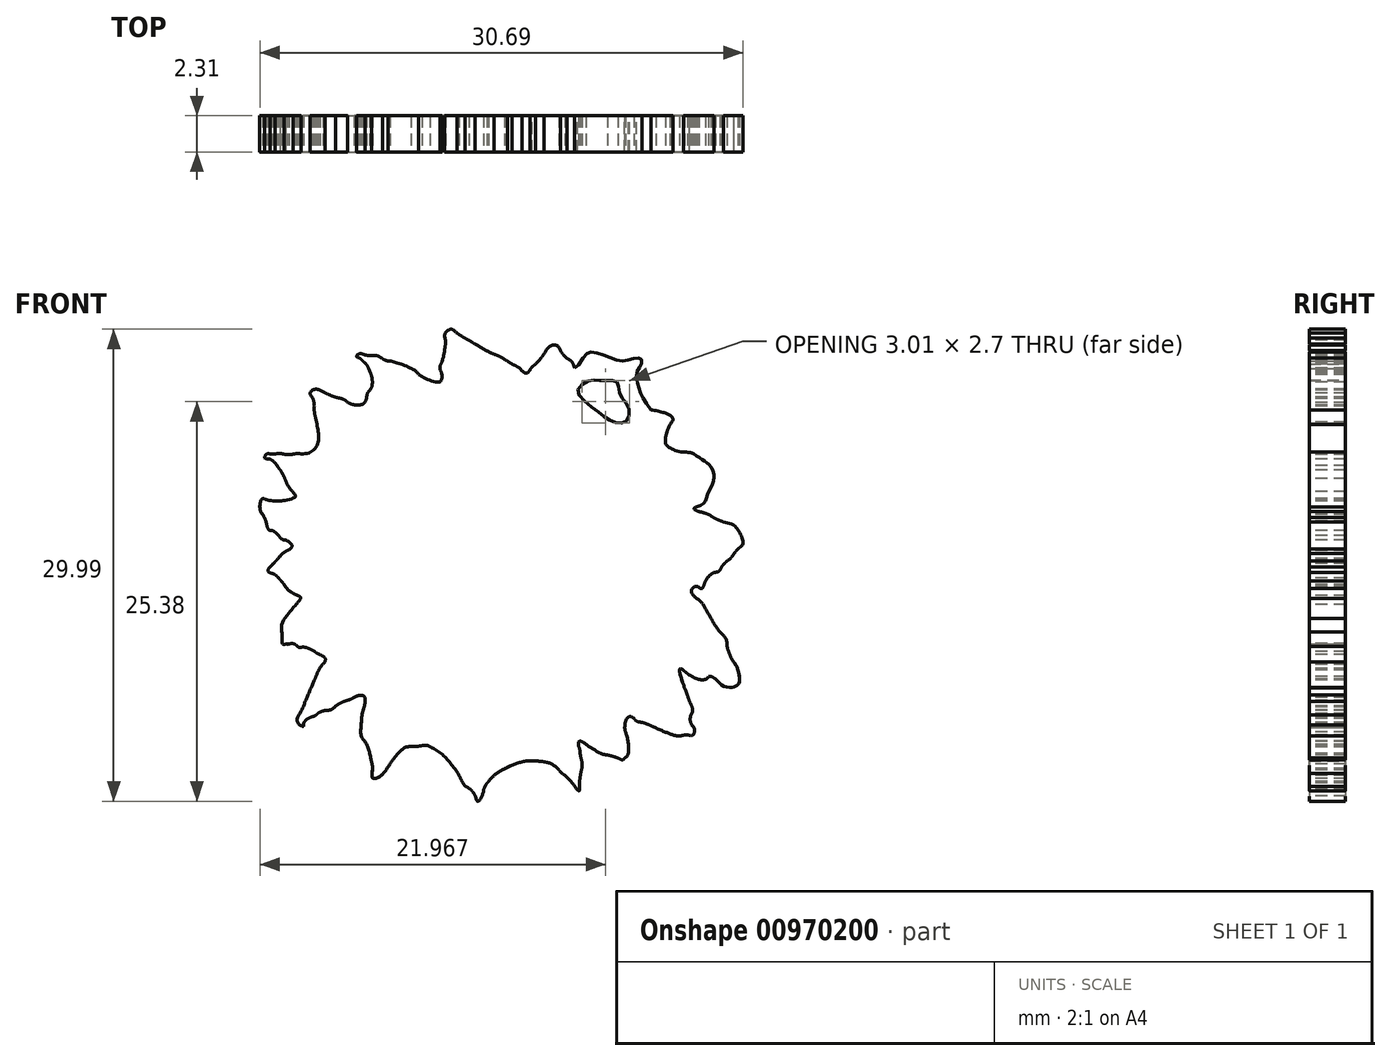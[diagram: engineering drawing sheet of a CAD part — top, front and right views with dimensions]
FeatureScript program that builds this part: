
annotation { "Feature Type Name" : "Feature", "Feature Type Description" : "" }
export const myFeature = defineFeature(function(context is Context, id is Id, definition is map)
    precondition{}
    {
        {
            var Q0;
            Q0=qCreatedBy(makeId("Front.planeOp"),FACE);
            var sketch = newSketch(context, id + "F0", { "sketchPlane" : qUnion([Q0])});
            skFitSpline(sketch, "E0", {"points": [v(2.12, 9.55) * mm, v(2.44, 9.4) * mm, v(2.83, 9.1) * mm, v(3.27, 8.7) * mm, v(3.44, 8.3) * mm, v(3.76, 7.75) * mm, v(3.76, 7.23) * mm, v(3.37, 6.8) * mm, v(2.85, 6.34) * mm, v(2.33, 5.86) * mm, v(1.64, 5.47) * mm, v(1.23, 5.23) * mm, v(0.6, 5.34) * mm, v(0.01, 5.58) * mm, v(-0.53, 5.65) * mm, v(-1, 5.84) * mm, v(-1.7, 6.08) * mm, v(-2.35, 6.32) * mm, v(-2.79, 6.5) * mm, v(-2.7, 6.82) * mm, v(-2.27, 7.1) * mm, v(-1.72, 7.4) * mm, v(-1.1, 7.27) * mm, v(-0.1, 7) * mm, v(0.92, 6.45) * mm, v(1.55, 6.32) * mm, v(2.16, 6.51) * mm, v(2.29, 6.88) * mm, v(1.9, 7.36) * mm, v(1.55, 7.66) * mm, v(1.25, 8.23) * mm, v(1.03, 8.62) * mm, v(1.03, 8.99) * mm, v(1.33, 9.18) * mm, v(1.86, 9.36) * mm, v(2.12, 9.55) * mm]});
            skFitSpline(sketch, "E1", {"points": [v(5.07, 10.48) * mm, v(5.98, 10.53) * mm, v(6.8, 10.57) * mm, v(7.37, 10.6) * mm, v(7.86, 10.57) * mm, v(8.45, 10.53) * mm, v(9.01, 10.61) * mm, v(9.66, 10.48) * mm, v(10.1, 10.33) * mm, v(10.1, 9.8) * mm, v(10.06, 9.07) * mm, v(9.86, 8.64) * mm, v(9.45, 8.62) * mm, v(8.69, 8.84) * mm, v(8.12, 8.88) * mm, v(7.3, 8.88) * mm, v(6.45, 8.73) * mm, v(5.76, 8.58) * mm, v(5.33, 8.36) * mm, v(4.76, 8.1) * mm, v(4.63, 8.53) * mm, v(4.35, 8.9) * mm, v(4.02, 9.31) * mm, v(3.76, 9.7) * mm, v(3.72, 10.07) * mm, v(4, 10.27) * mm, v(4.55, 10.38) * mm, v(5.07, 10.48) * mm]});
            skFitSpline(sketch, "E2", {"points": [v(3.8, 5.84) * mm, v(3.42, 5.5) * mm, v(3.11, 5.02) * mm, v(2.74, 4.7) * mm, v(2.81, 4.35) * mm, v(3.29, 4.04) * mm, v(3.85, 3.8) * mm, v(4.5, 3.48) * mm, v(5.17, 3.28) * mm, v(5.63, 3.15) * mm, v(5.98, 3.46) * mm, v(6.28, 3.59) * mm, v(6.41, 3.76) * mm, v(6.22, 4.28) * mm, v(5.67, 4.8) * mm, v(5.41, 5.32) * mm, v(5.02, 5.84) * mm, v(4.78, 6.15) * mm, v(4.46, 6.28) * mm, v(3.8, 5.84) * mm]});
            skFitSpline(sketch, "E3", {"points": [v(7.84, 7.7) * mm, v(8.28, 7.8) * mm, v(9.08, 7.64) * mm, v(9.64, 7.37) * mm, v(9.73, 6.97) * mm, v(9.58, 6.5) * mm, v(9.45, 5.82) * mm, v(9.32, 5.32) * mm, v(9.25, 4.87) * mm, v(9.23, 4.32) * mm, v(9.08, 3.8) * mm, v(8.88, 3.5) * mm, v(8.4, 3.43) * mm, v(8.02, 3.85) * mm, v(7.5, 4.54) * mm, v(7.08, 5.06) * mm, v(6.56, 5.71) * mm, v(6.26, 6.38) * mm, v(6.04, 6.9) * mm, v(6.28, 7.23) * mm, v(6.54, 7.47) * mm, v(7.15, 7.7) * mm, v(7.84, 7.7) * mm]});
            skFitSpline(sketch, "E4", {"points": [v(12.28, 5.84) * mm, v(13.03, 5.31) * mm, v(13.8, 4.47) * mm, v(14.16, 4.05) * mm, v(13.98, 3.67) * mm, v(13, 3.38) * mm, v(12.17, 2.87) * mm, v(11.6, 2.58) * mm, v(10.93, 2.43) * mm, v(10.57, 2.67) * mm, v(10.35, 2.9) * mm, v(10.31, 3.45) * mm, v(10.28, 4.15) * mm, v(10.57, 4.84) * mm, v(10.72, 5.84) * mm, v(10.86, 6.5) * mm, v(11.04, 7.03) * mm, v(11.28, 6.8) * mm, v(11.85, 6.24) * mm, v(12.28, 5.84) * mm]});
            skFitSpline(sketch, "E5", {"points": [v(14.32, 7.37) * mm, v(14.83, 6.85) * mm, v(15.37, 6.41) * mm, v(15.91, 5.84) * mm, v(16.35, 5.11) * mm, v(16.6, 4.9) * mm, v(16.41, 4.62) * mm, v(16.08, 4.6) * mm, v(15.46, 4.65) * mm, v(15.14, 4.6) * mm, v(14.71, 5) * mm, v(14.36, 5.47) * mm, v(13.76, 6.01) * mm, v(13.23, 6.45) * mm, v(12.6, 6.93) * mm, v(11.99, 7.37) * mm, v(11.59, 7.7) * mm, v(11.16, 7.94) * mm, v(10.98, 8.06) * mm, v(10.96, 8.53) * mm, v(11.1, 9.02) * mm, v(11.18, 9.34) * mm, v(11.32, 9.77) * mm, v(11.56, 9.74) * mm, v(11.86, 9.4) * mm, v(12.38, 8.9) * mm, v(13.28, 8.14) * mm, v(13.77, 7.78) * mm, v(14.32, 7.37) * mm]});
            skFitSpline(sketch, "E6", {"points": [v(17.5, 2.4) * mm, v(17.3, 3) * mm, v(17.24, 3.43) * mm, v(17.05, 3.69) * mm, v(16.73, 3.76) * mm, v(16.3, 3.41) * mm, v(16.43, 3.03) * mm, v(16.62, 2.37) * mm, v(16.76, 1.68) * mm, v(16.9, 0.97) * mm, v(16.6, 0.3) * mm, v(16.43, -0.36) * mm, v(16.25, -1.1) * mm, v(16.25, -1.77) * mm, v(15.87, -2.4) * mm, v(15.65, -3.32) * mm, v(15.5, -3.8) * mm, v(15.52, -4.34) * mm, v(15.83, -4.7) * mm, v(16.16, -5.01) * mm, v(16.65, -5.45) * mm, v(17.04, -5.74) * mm, v(17.15, -5.2) * mm, v(17.38, -4.58) * mm, v(17.53, -3.85) * mm, v(17.55, -3.08) * mm, v(17.62, -2.44) * mm, v(17.67, -1.7) * mm, v(17.7, -1.26) * mm, v(17.82, -0.62) * mm, v(17.93, -0.22) * mm, v(17.91, 0.64) * mm, v(17.75, 1.48) * mm, v(17.5, 2.4) * mm]});
            skFitSpline(sketch, "E7", {"points": [v(12.84, 1.74) * mm, v(13.64, 2.13) * mm, v(14.11, 2.34) * mm, v(14.65, 2.65) * mm, v(14.76, 2.27) * mm, v(15, 1.18) * mm, v(15.14, 0.21) * mm, v(15.26, 0) * mm, v(15.22, -0.92) * mm, v(15.03, -1.58) * mm, v(14.88, -1.83) * mm, v(14.3, -2.35) * mm, v(13.84, -2.75) * mm, v(13.62, -2.84) * mm, v(12.6, -2.35) * mm, v(11.63, -1.65) * mm, v(10.97, -1.05) * mm, v(11.12, -0.48) * mm, v(11.1, 0) * mm, v(10.98, 0.47) * mm, v(11.48, 1) * mm, v(12.04, 1.42) * mm, v(12.84, 1.74) * mm]});
            skFitSpline(sketch, "E8", {"points": [v(10.72, -3.9) * mm, v(11.12, -4.64) * mm, v(11.32, -5.11) * mm, v(11.41, -5.53) * mm, v(11.81, -5.68) * mm, v(12.3, -5.53) * mm, v(12.65, -5.3) * mm, v(12.94, -4.8) * mm, v(13.13, -4.3) * mm, v(12.85, -3.98) * mm, v(12.67, -3.76) * mm, v(12.1, -3.36) * mm, v(11.37, -2.92) * mm, v(10.68, -2.49) * mm, v(10.13, -2.38) * mm, v(10.32, -3.09) * mm, v(10.72, -3.9) * mm]});
            skFitSpline(sketch, "E9", {"points": [v(9.2, -4.22) * mm, v(9.42, -4.82) * mm, v(9.64, -5.68) * mm, v(9.59, -6.32) * mm, v(9.24, -6.5) * mm, v(8.42, -6.48) * mm, v(7.73, -6.37) * mm, v(6.87, -6.3) * mm, v(6.32, -5.99) * mm, v(6.47, -5.37) * mm, v(6.76, -5) * mm, v(7.03, -4.47) * mm, v(7.05, -3.84) * mm, v(7.34, -3.16) * mm, v(7.64, -2.56) * mm, v(8.02, -2.18) * mm, v(8.26, -2.12) * mm, v(8.58, -2.65) * mm, v(8.58, -3.23) * mm, v(9.1, -3.49) * mm, v(9.15, -3.82) * mm, v(9.2, -4.22) * mm]});
            skFitSpline(sketch, "E10", {"points": [v(5.92, -3.22) * mm, v(5.63, -3.84) * mm, v(5.15, -4.33) * mm, v(4.9, -4.64) * mm, v(4.6, -4.6) * mm, v(4.2, -4.2) * mm, v(3.71, -3.63) * mm, v(3.17, -3.09) * mm, v(2.86, -2.69) * mm, v(2.5, -2.3) * mm, v(2.36, -2.01) * mm, v(2.66, -1.83) * mm, v(3.07, -1.77) * mm, v(3.66, -1.48) * mm, v(4.11, -1.15) * mm, v(4.59, -0.9) * mm, v(5.35, -0.75) * mm, v(5.56, -0.75) * mm, v(6.03, -1.08) * mm, v(6.5, -1.43) * mm, v(6.78, -1.8) * mm, v(6.43, -2.16) * mm, v(6.32, -2.58) * mm, v(5.92, -3.22) * mm]});
            skFitSpline(sketch, "E11", {"points": [v(3.13, 3) * mm, v(3.84, 2.7) * mm, v(4.6, 2.35) * mm, v(4.7, 2) * mm, v(4.84, 1.55) * mm, v(5.06, 1.27) * mm, v(4.77, 0.8) * mm, v(4.26, 0.49) * mm, v(3.68, 0.2) * mm, v(2.97, -0.31) * mm, v(2.44, -0.55) * mm, v(1.78, -0.73) * mm, v(1.7, -0.31) * mm, v(1.8, 0) * mm, v(1.83, 0.38) * mm, v(1.96, 0.8) * mm, v(2.05, 1.35) * mm, v(2.13, 1.98) * mm, v(2.03, 2.28) * mm, v(2.22, 2.68) * mm, v(2.3, 3.02) * mm, v(2.36, 3.24) * mm, v(2.78, 3.24) * mm, v(3.13, 3) * mm]});
            skFitSpline(sketch, "E12", {"points": [v(-1.32, 5.03) * mm, v(-0.7, 4.76) * mm, v(-0.23, 4.45) * mm, v(0.56, 3.97) * mm, v(0.98, 3.55) * mm, v(1.01, 3.13) * mm, v(1.03, 2.22) * mm, v(0.81, 1.5) * mm, v(0.69, 0.85) * mm, v(0.6, 0.58) * mm, v(0.54, 0.34) * mm, v(0.5, -0.15) * mm, v(0.5, -0.63) * mm, v(0.72, -0.86) * mm, v(0.43, -1.32) * mm, v(0, -1.68) * mm, v(-0.37, -2.05) * mm, v(-1.18, -2.34) * mm, v(-1.65, -2.49) * mm, v(-2.2, -2.76) * mm, v(-2.82, -3.03) * mm, v(-3.14, -3.06) * mm, v(-3.36, -2.79) * mm, v(-3.25, -2.59) * mm, v(-3, -2.33) * mm, v(-2.54, -2.1) * mm, v(-1.97, -1.71) * mm, v(-1.71, -1.46) * mm, v(-1.59, -1.17) * mm, v(-1.13, -0.78) * mm, v(-0.88, -0.67) * mm, v(-0.77, -0.47) * mm, v(-1.2, -0.2) * mm, v(-1.79, 0) * mm, v(-2.39, 0.11) * mm, v(-2.74, 0.33) * mm, v(-3.1, 0.51) * mm, v(-3.17, 0.8) * mm, v(-3.16, 1) * mm, v(-3.32, 1.22) * mm, v(-3.05, 1.5) * mm, v(-2.5, 1.8) * mm, v(-2, 1.94) * mm, v(-1.64, 2.15) * mm, v(-1.33, 2.56) * mm, v(-1.42, 2.88) * mm, v(-1.93, 3.25) * mm, v(-2.77, 3.54) * mm, v(-3.05, 3.76) * mm, v(-3.17, 4.03) * mm, v(-3.4, 4.25) * mm, v(-3.69, 4.6) * mm, v(-3.65, 5.15) * mm, v(-3.3, 5.44) * mm, v(-2.65, 5.58) * mm, v(-1.93, 5.22) * mm, v(-1.32, 5.03) * mm]});
            skFitSpline(sketch, "E13", {"points": [v(-1.89, -5.5) * mm, v(-1.15, -5.1) * mm, v(-0.26, -4.5) * mm, v(0.67, -4.07) * mm, v(1.03, -4.02) * mm, v(1.39, -4.46) * mm, v(1.5, -5.15) * mm, v(1.32, -5.87) * mm, v(1.3, -6.73) * mm, v(1.06, -7.86) * mm, v(1.28, -8.34) * mm, v(2.06, -8.8) * mm, v(2.5, -9.01) * mm, v(2.9, -8.5) * mm, v(3.39, -7.62) * mm, v(3.62, -6.9) * mm, v(3.15, -5.95) * mm, v(2.58, -4.9) * mm, v(2.13, -4.05) * mm, v(1.6, -3.3) * mm, v(1.1, -2.72) * mm, v(0.22, -2.4) * mm, v(-0.52, -2.74) * mm, v(-1.3, -3.33) * mm, v(-2.17, -3.9) * mm, v(-2.4, -4.28) * mm, v(-2.32, -5.02) * mm, v(-1.89, -5.5) * mm]});
            skFitSpline(sketch, "E14", {"points": [v(8.43, -8.06) * mm, v(9.05, -8.35) * mm, v(9.56, -8.44) * mm, v(10.13, -8.71) * mm, v(10.13, -9.33) * mm, v(10.13, -10.23) * mm, v(9.7, -10.76) * mm, v(9.2, -11.08) * mm, v(8.29, -11.05) * mm, v(7.61, -11) * mm, v(7.36, -10.06) * mm, v(7.23, -9.04) * mm, v(7.23, -8.22) * mm, v(7.23, -7.7) * mm, v(7.63, -7.91) * mm, v(8.07, -8.1) * mm, v(8.43, -8.06) * mm]});
            skFitSpline(sketch, "E15", {"points": [v(6.57, -7.67) * mm, v(6.2, -8.51) * mm, v(5.8, -9.3) * mm, v(5.53, -10) * mm, v(5.28, -10.36) * mm, v(4.59, -10.17) * mm, v(3.94, -9.92) * mm, v(3.84, -9.04) * mm, v(4.11, -8.44) * mm, v(4.91, -7.73) * mm, v(5.5, -7.47) * mm, v(6.57, -7.67) * mm]});
            skFitSpline(sketch, "E16", {"points": [v(13.72, -6.2) * mm, v(13.03, -6.42) * mm, v(12.3, -6.82) * mm, v(11.88, -7.3) * mm, v(11.72, -8.1) * mm, v(11.79, -8.66) * mm, v(11.79, -9.44) * mm, v(11.9, -9.88) * mm, v(12.24, -9.64) * mm, v(12.63, -9.32) * mm, v(13.1, -9.39) * mm, v(13.52, -9.33) * mm, v(14.16, -8.86) * mm, v(15, -8.28) * mm, v(15.04, -8.02) * mm, v(15.5, -7.67) * mm, v(15.8, -7.38) * mm, v(15.87, -6.78) * mm, v(15.86, -6.4) * mm, v(15.33, -5.92) * mm, v(14.82, -5.81) * mm, v(14.16, -6.05) * mm, v(13.72, -6.2) * mm]});
            skFitSpline(sketch, "E17", {"points": [v(15.2, -12.36) * mm, v(15.31, -11.07) * mm, v(15.2, -10.5) * mm, v(15.2, -10.4) * mm, v(15.28, -9.97) * mm, v(15.55, -9.74) * mm, v(15.93, -9.96) * mm, v(16.4, -10.14) * mm, v(17.25, -10.49) * mm, v(17.94, -10.78) * mm, v(18.34, -10.9) * mm, v(18.78, -10.94) * mm, v(19.13, -10.9) * mm, v(19.44, -10.87) * mm, v(19.55, -10.54) * mm, v(19.36, -10) * mm, v(19.44, -9.4) * mm, v(19.33, -8.8) * mm, v(19.14, -8.28) * mm, v(18.87, -7.53) * mm, v(18.7, -6.7) * mm, v(19.2, -6.93) * mm, v(20.4, -7.24) * mm, v(20.66, -7.18) * mm, v(21.46, -7.62) * mm, v(22.3, -7.59) * mm, v(22.43, -7.15) * mm, v(22.23, -6.5) * mm, v(21.83, -5.69) * mm, v(21.57, -4.86) * mm, v(21.15, -4.24) * mm, v(20.73, -3.58) * mm, v(20.3, -2.89) * mm, v(19.83, -2.3) * mm, v(19.43, -1.8) * mm, v(19.65, -1.48) * mm, v(20.01, -1.48) * mm, v(20.42, -1) * mm, v(20.8, -0.63) * mm, v(21.15, -0.46) * mm, v(21.47, -0.08) * mm, v(21.86, 0.29) * mm, v(22.33, 0.83) * mm, v(22.62, 1.3) * mm, v(22.51, 1.82) * mm, v(22.02, 2.37) * mm, v(21.1, 2.77) * mm, v(20.32, 3.13) * mm, v(19.61, 3.46) * mm, v(20, 3.73) * mm, v(20.42, 4.26) * mm, v(20.74, 5.07) * mm, v(20.78, 5.72) * mm, v(20.45, 6.3) * mm, v(19.98, 6.67) * mm, v(19.38, 6.96) * mm, v(18.56, 7.13) * mm, v(18, 7.36) * mm, v(17.8, 7.58) * mm, v(17.8, 8.02) * mm, v(18, 8.68) * mm, v(18.2, 9.15) * mm, v(18.06, 9.37) * mm, v(17.72, 9.54) * mm, v(16.88, 9.7) * mm, v(16.06, 9.7) * mm, v(15.03, 9.66) * mm, v(14.34, 9.55) * mm, v(13.67, 9.55) * mm, v(13.4, 9.8) * mm, v(12.77, 10.63) * mm, v(12.35, 11.52) * mm, v(12.08, 12.16) * mm, v(11.77, 12.76) * mm, v(11.26, 13.3) * mm, v(10.97, 13.7) * mm, v(10.64, 13.79) * mm, v(10.24, 13.51) * mm, v(9.95, 13.11) * mm, v(9.58, 12.7) * mm, v(9.23, 12.33) * mm, v(8.96, 12.07) * mm, v(8.6, 12.29) * mm, v(8.01, 12.67) * mm, v(7.36, 13.06) * mm, v(6.55, 13.44) * mm, v(5.68, 13.93) * mm, v(5.06, 14.3) * mm, v(4.62, 14.57) * mm, v(4.22, 14.8) * mm, v(3.98, 14.75) * mm, v(3.82, 14.5) * mm, v(3.82, 14.04) * mm, v(3.78, 13.64) * mm, v(3.65, 12.98) * mm, v(3.52, 12.38) * mm, v(3.6, 11.96) * mm, v(3.56, 11.65) * mm, v(3.36, 11.5) * mm, v(2.36, 11.83) * mm, v(1.83, 12.18) * mm, v(0.33, 12.8) * mm, v(-0.03, 12.9) * mm, v(-0.54, 13.13) * mm, v(-1.13, 13.2) * mm, v(-1.64, 13.25) * mm, v(-1.76, 13.14) * mm, v(-1.6, 13) * mm, v(-1.42, 12.84) * mm, v(-1.16, 12.56) * mm, v(-0.98, 12.18) * mm, v(-0.87, 11.89) * mm, v(-0.85, 11.23) * mm, v(-1.05, 10.85) * mm, v(-1.25, 10.3) * mm, v(-1.46, 10.1) * mm, v(-2.08, 10.08) * mm, v(-2.62, 10.34) * mm, v(-3.44, 10.65) * mm, v(-4.03, 10.9) * mm, v(-4.54, 10.96) * mm, v(-4.7, 10.76) * mm, v(-4.57, 10.4) * mm, v(-4.5, 9.85) * mm, v(-4.37, 9) * mm, v(-4.26, 8.37) * mm, v(-4.25, 7.84) * mm, v(-4.43, 7.35) * mm, v(-4.9, 7) * mm, v(-5.6, 6.94) * mm, v(-6.14, 6.9) * mm, v(-6.8, 6.94) * mm, v(-7.27, 6.93) * mm, v(-7.46, 6.93) * mm, v(-7.57, 6.74) * mm, v(-7.22, 6.56) * mm, v(-6.85, 6.18) * mm, v(-6.56, 5.74) * mm, v(-6.34, 5.3) * mm, v(-5.98, 4.68) * mm, v(-5.72, 4.32) * mm, v(-5.76, 4.2) * mm, v(-6.4, 3.99) * mm, v(-6.95, 3.95) * mm, v(-7.55, 4.03) * mm, v(-7.75, 4.08) * mm, v(-7.86, 3.97) * mm, v(-7.88, 3.35) * mm, v(-7.68, 2.88) * mm, v(-7.33, 2.18) * mm, v(-7.02, 1.98) * mm, v(-6.58, 1.6) * mm, v(-6.18, 1.4) * mm, v(-5.92, 1.13) * mm, v(-6.03, 0.93) * mm, v(-6.44, 0.65) * mm, v(-6.84, 0.27) * mm, v(-7.24, -0.17) * mm, v(-7.4, -0.46) * mm, v(-7.31, -0.59) * mm, v(-7.02, -0.72) * mm, v(-6.76, -0.95) * mm, v(-6.53, -1.23) * mm, v(-6.25, -1.57) * mm, v(-5.87, -1.88) * mm, v(-5.52, -2.07) * mm, v(-5.38, -2.2) * mm, v(-5.64, -2.6) * mm, v(-6, -3.04) * mm, v(-6.48, -3.88) * mm, v(-6.55, -4.62) * mm, v(-6.45, -5.09) * mm, v(-6.3, -5.13) * mm, v(-6.16, -5.13) * mm, v(-5.85, -5.11) * mm, v(-5.5, -5.28) * mm, v(-5.07, -5.35) * mm, v(-4.56, -5.57) * mm, v(-4.2, -5.77) * mm, v(-3.84, -6) * mm, v(-3.83, -6.23) * mm, v(-4.06, -6.57) * mm, v(-4.43, -7.27) * mm, v(-4.7, -7.89) * mm, v(-5.05, -8.69) * mm, v(-5.3, -9.34) * mm, v(-5.45, -10.07) * mm, v(-5.25, -10.26) * mm, v(-5.12, -10.04) * mm, v(-4.52, -9.67) * mm, v(-4.06, -9.42) * mm, v(-3.5, -9.25) * mm, v(-2.9, -8.9) * mm, v(-2.2, -8.61) * mm, v(-1.62, -8.4) * mm, v(-1.3, -8.5) * mm, v(-1.36, -9.22) * mm, v(-1.5, -10.27) * mm, v(-1.44, -11) * mm, v(-1.1, -11.73) * mm, v(-0.89, -12.57) * mm, v(-0.82, -12.94) * mm, v(-0.73, -13.55) * mm, v(-0.5, -13.58) * mm, v(-0.11, -13.3) * mm, v(0.24, -12.83) * mm, v(0.44, -12.54) * mm, v(1, -11.88) * mm, v(1.4, -11.66) * mm, v(1.88, -11.62) * mm, v(2.58, -11.57) * mm, v(2.7, -11.59) * mm, v(2.92, -11.7) * mm, v(3.56, -12.1) * mm, v(4.07, -12.63) * mm, v(4.56, -13.28) * mm, v(5.13, -14.1) * mm, v(5.6, -14.6) * mm, v(5.88, -14.94) * mm, v(6.15, -14.63) * mm, v(6.33, -14.16) * mm, v(6.5, -13.92) * mm, v(6.9, -13.49) * mm, v(7.52, -13.08) * mm, v(8.12, -12.8) * mm, v(9, -12.56) * mm, v(9.5, -12.56) * mm, v(10.53, -12.74) * mm, v(11.15, -13.25) * mm, v(11.59, -13.65) * mm, v(12.13, -14.29) * mm, v(12.28, -14.4) * mm, v(12.32, -14.23) * mm, v(12.35, -13.7) * mm, v(12.43, -13.23) * mm, v(12.46, -12.68) * mm, v(12.39, -12.2) * mm, v(12.32, -11.77) * mm, v(12.26, -11.4) * mm, v(12.37, -11.3) * mm, v(12.75, -11.5) * mm, v(13.28, -11.84) * mm, v(13.83, -12.1) * mm, v(14.62, -12.32) * mm, v(15.2, -12.36) * mm]});
            skSolve(sketch);
        }
        {
            var Q0;
            Q0 = qSketchRegion(id + "F0", true);
            extrude(context, id + "F1", {"entities" : qUnion([Q0]), "depth" : 2.3 * mm, "offsetDistance" : 25.4 * mm});
        }
        {
            var Q0;
            Q0=makeQuery(id+"F1.opExtrude","CAP_FACE",FACE,{"disambiguationData":[OSD([sQuery(id+"F0.wireOp",EDGE,"E0"),sQuery(id+"F0.wireOp",EDGE,"E1"),sQuery(id+"F0.wireOp",EDGE,"E2"),sQuery(id+"F0.wireOp",EDGE,"E3"),sQuery(id+"F0.wireOp",EDGE,"E4"),sQuery(id+"F0.wireOp",EDGE,"E5"),sQuery(id+"F0.wireOp",EDGE,"E6"),sQuery(id+"F0.wireOp",EDGE,"E7"),sQuery(id+"F0.wireOp",EDGE,"E8"),sQuery(id+"F0.wireOp",EDGE,"E9"),sQuery(id+"F0.wireOp",EDGE,"E10"),sQuery(id+"F0.wireOp",EDGE,"E11"),sQuery(id+"F0.wireOp",EDGE,"E12"),sQuery(id+"F0.wireOp",EDGE,"E13"),sQuery(id+"F0.wireOp",EDGE,"E14"),sQuery(id+"F0.wireOp",EDGE,"E15"),sQuery(id+"F0.wireOp",EDGE,"E16"),sQuery(id+"F0.wireOp",EDGE,"E17")])],"isStart":false});
            var sketch = newSketch(context, id + "F2", { "sketchPlane" : qUnion([Q0])});
            skFitSpline(sketch, "E18", {"points": [v(11.95, 12.45) * mm, v(12.5, 12.99) * mm, v(13.04, 13.4) * mm, v(14, 13.18) * mm, v(15.06, 12.85) * mm, v(15.8, 13.02) * mm, v(16.25, 12.96) * mm, v(16.25, 12.63) * mm, v(15.96, 12.12) * mm, v(16.07, 11.29) * mm, v(16.27, 10.7) * mm, v(16.89, 9.7) * mm], "startDerivative": vector(3.57, -8.3) * mm, "endDerivative": vector(6.38, -9.46) * mm});
            skFitSpline(sketch, "E19.0", {"points": [v(15.2, -12.36) * mm, v(15.4, -12.18) * mm, v(15.36, -11.06) * mm, v(15.2, -10.52) * mm, v(15.2, -10.4) * mm, v(15.22, -9.95) * mm, v(15.56, -9.62) * mm, v(15.94, -10.02) * mm, v(16.42, -10.12) * mm, v(17.24, -10.49) * mm, v(17.93, -10.78) * mm, v(18.33, -10.92) * mm, v(18.78, -10.96) * mm, v(19.11, -10.88) * mm, v(19.48, -10.94) * mm, v(19.62, -10.5) * mm, v(19.25, -10) * mm, v(19.5, -9.4) * mm, v(19.33, -8.8) * mm, v(19.14, -8.25) * mm, v(18.88, -7.62) * mm, v(18.54, -6.45) * mm, v(19.22, -7.03) * mm, v(20.4, -7.34) * mm, v(20.66, -7.06) * mm, v(21.41, -7.76) * mm, v(22.4, -7.7) * mm, v(22.47, -7.12) * mm, v(22.25, -6.46) * mm, v(21.76, -5.71) * mm, v(21.64, -4.83) * mm, v(21.12, -4.25) * mm, v(20.72, -3.58) * mm, v(20.32, -2.87) * mm, v(19.89, -2.3) * mm, v(19.28, -1.84) * mm, v(19.63, -1.38) * mm, v(20.07, -1.62) * mm, v(20.4, -0.95) * mm, v(20.77, -0.6) * mm, v(21.18, -0.51) * mm, v(21.46, -0.04) * mm, v(21.88, 0.27) * mm, v(22.32, 0.83) * mm, v(22.71, 1.26) * mm, v(22.54, 1.86) * mm, v(22.07, 2.44) * mm, v(21.06, 2.74) * mm, v(20.45, 3.13) * mm, v(19.31, 3.44) * mm, v(20.1, 3.72) * mm, v(20.43, 4.25) * mm, v(20.78, 5.05) * mm, v(20.86, 5.73) * mm, v(20.48, 6.34) * mm, v(19.98, 6.68) * mm, v(19.4, 7.02) * mm, v(18.56, 7.08) * mm, v(18.01, 7.34) * mm, v(17.76, 7.57) * mm, v(17.8, 8.05) * mm, v(17.97, 8.67) * mm, v(18.27, 9.14) * mm, v(18.06, 9.4) * mm, v(17.7, 9.56) * mm, v(16.85, 9.74) * mm, v(16.08, 9.69) * mm, v(15.02, 9.7) * mm, v(14.39, 9.54) * mm, v(13.63, 9.49) * mm, v(13.39, 9.8) * mm, v(12.7, 10.62) * mm, v(12.37, 11.51) * mm, v(12.08, 12.15) * mm, v(11.83, 12.8) * mm, v(11.22, 13.25) * mm, v(11.02, 13.73) * mm, v(10.62, 13.85) * mm, v(10.2, 13.52) * mm, v(9.96, 13.1) * mm, v(9.58, 12.68) * mm, v(9.24, 12.36) * mm, v(8.97, 11.94) * mm, v(8.58, 12.34) * mm, v(8, 12.67) * mm, v(7.36, 13.08) * mm, v(6.54, 13.42) * mm, v(5.7, 13.92) * mm, v(5.07, 14.3) * mm, v(4.63, 14.55) * mm, v(4.24, 14.86) * mm, v(3.96, 14.77) * mm, v(3.76, 14.5) * mm, v(3.84, 14.03) * mm, v(3.78, 13.64) * mm, v(3.67, 12.98) * mm, v(3.46, 12.4) * mm, v(3.63, 11.98) * mm, v(3.59, 11.64) * mm, v(3.36, 11.4) * mm, v(2.25, 11.83) * mm, v(1.93, 12.2) * mm, v(0.32, 12.83) * mm, v(-0.01, 12.87) * mm, v(-0.55, 13.19) * mm, v(-1.1, 13.17) * mm, v(-1.62, 13.31) * mm, v(-1.83, 13.12) * mm, v(-1.58, 13.01) * mm, v(-1.42, 12.83) * mm, v(-1.13, 12.58) * mm, v(-0.98, 12.17) * mm, v(-0.85, 11.9) * mm, v(-0.78, 11.19) * mm, v(-1.09, 10.89) * mm, v(-1.23, 10.28) * mm, v(-1.43, 10.05) * mm, v(-2.13, 10.02) * mm, v(-2.6, 10.38) * mm, v(-3.46, 10.62) * mm, v(-3.98, 10.92) * mm, v(-4.54, 11.03) * mm, v(-4.78, 10.75) * mm, v(-4.52, 10.38) * mm, v(-4.52, 9.84) * mm, v(-4.38, 9) * mm, v(-4.26, 8.38) * mm, v(-4.21, 7.84) * mm, v(-4.38, 7.31) * mm, v(-4.88, 6.92) * mm, v(-5.6, 6.97) * mm, v(-6.14, 6.88) * mm, v(-6.78, 6.98) * mm, v(-7.26, 6.9) * mm, v(-7.46, 6.98) * mm, v(-7.68, 6.68) * mm, v(-7.15, 6.6) * mm, v(-6.86, 6.18) * mm, v(-6.54, 5.74) * mm, v(-6.35, 5.3) * mm, v(-6.02, 4.7) * mm, v(-5.7, 4.34) * mm, v(-5.73, 4.14) * mm, v(-6.44, 3.96) * mm, v(-6.91, 3.94) * mm, v(-7.54, 4) * mm, v(-7.75, 4.12) * mm, v(-7.9, 3.97) * mm, v(-7.92, 3.3) * mm, v(-7.66, 2.92) * mm, v(-7.39, 2.11) * mm, v(-7, 2.03) * mm, v(-6.6, 1.54) * mm, v(-6.19, 1.45) * mm, v(-5.85, 1.14) * mm, v(-6.03, 0.9) * mm, v(-6.47, 0.67) * mm, v(-6.83, 0.27) * mm, v(-7.23, -0.14) * mm, v(-7.45, -0.45) * mm, v(-7.31, -0.62) * mm, v(-7, -0.69) * mm, v(-6.76, -0.96) * mm, v(-6.52, -1.22) * mm, v(-6.27, -1.6) * mm, v(-5.88, -1.9) * mm, v(-5.54, -2.06) * mm, v(-5.28, -2.18) * mm, v(-5.68, -2.64) * mm, v(-6, -3.02) * mm, v(-6.57, -3.86) * mm, v(-6.56, -4.57) * mm, v(-6.52, -5.13) * mm, v(-6.29, -5.13) * mm, v(-6.16, -5.14) * mm, v(-5.82, -5.05) * mm, v(-5.51, -5.33) * mm, v(-5.06, -5.3) * mm, v(-4.54, -5.57) * mm, v(-4.24, -5.77) * mm, v(-3.8, -5.96) * mm, v(-3.8, -6.26) * mm, v(-4.1, -6.57) * mm, v(-4.44, -7.28) * mm, v(-4.7, -7.87) * mm, v(-5.06, -8.7) * mm, v(-5.28, -9.3) * mm, v(-5.59, -10.06) * mm, v(-5.2, -10.35) * mm, v(-5.18, -9.95) * mm, v(-4.48, -9.7) * mm, v(-4.1, -9.37) * mm, v(-3.46, -9.3) * mm, v(-2.91, -8.86) * mm, v(-2.2, -8.64) * mm, v(-1.66, -8.34) * mm, v(-1.18, -8.46) * mm, v(-1.4, -9.27) * mm, v(-1.54, -10.26) * mm, v(-1.5, -11.03) * mm, v(-1.04, -11.69) * mm, v(-0.9, -12.59) * mm, v(-0.8, -12.9) * mm, v(-0.82, -13.63) * mm, v(-0.46, -13.61) * mm, v(-0.1, -13.3) * mm, v(0.25, -12.82) * mm, v(0.43, -12.54) * mm, v(0.98, -11.84) * mm, v(1.38, -11.62) * mm, v(1.86, -11.64) * mm, v(2.57, -11.56) * mm, v(2.7, -11.58) * mm, v(2.95, -11.7) * mm, v(3.61, -12.08) * mm, v(4.08, -12.63) * mm, v(4.58, -13.27) * mm, v(5.08, -14.15) * mm, v(5.62, -14.51) * mm, v(5.86, -15.12) * mm, v(6.2, -14.62) * mm, v(6.3, -14.15) * mm, v(6.5, -13.92) * mm, v(6.88, -13.44) * mm, v(7.53, -13.08) * mm, v(8.09, -12.77) * mm, v(9.02, -12.51) * mm, v(9.49, -12.56) * mm, v(10.6, -12.61) * mm, v(11.14, -13.27) * mm, v(11.6, -13.6) * mm, v(12.1, -14.26) * mm, v(12.3, -14.46) * mm, v(12.32, -14.2) * mm, v(12.34, -13.69) * mm, v(12.43, -13.24) * mm, v(12.5, -12.68) * mm, v(12.38, -12.21) * mm, v(12.34, -11.79) * mm, v(12.21, -11.41) * mm, v(12.38, -11.23) * mm, v(12.78, -11.52) * mm, v(13.28, -11.86) * mm, v(13.83, -12.13) * mm, v(14.58, -12.28) * mm, v(15.07, -12.49) * mm, v(15.2, -12.36) * mm]});
            skSolve(sketch);
        }
        {
            var Q0;
            Q0 = qSketchRegion(id + "F2", true);
            var Q1;
            Q1=makeQuery(id+"F1.opExtrude","CAP_FACE",FACE,{"disambiguationData":[OSD([sQuery(id+"F0.wireOp",EDGE,"E0"),sQuery(id+"F0.wireOp",EDGE,"E1"),sQuery(id+"F0.wireOp",EDGE,"E2"),sQuery(id+"F0.wireOp",EDGE,"E3"),sQuery(id+"F0.wireOp",EDGE,"E4"),sQuery(id+"F0.wireOp",EDGE,"E5"),sQuery(id+"F0.wireOp",EDGE,"E6"),sQuery(id+"F0.wireOp",EDGE,"E7"),sQuery(id+"F0.wireOp",EDGE,"E8"),sQuery(id+"F0.wireOp",EDGE,"E9"),sQuery(id+"F0.wireOp",EDGE,"E10"),sQuery(id+"F0.wireOp",EDGE,"E11"),sQuery(id+"F0.wireOp",EDGE,"E12"),sQuery(id+"F0.wireOp",EDGE,"E13"),sQuery(id+"F0.wireOp",EDGE,"E14"),sQuery(id+"F0.wireOp",EDGE,"E15"),sQuery(id+"F0.wireOp",EDGE,"E16"),sQuery(id+"F0.wireOp",EDGE,"E17")])],"isStart":true});
            extrude(context, id + "F3", {"entities" : qUnion([Q0]), "operationType" : NewBodyOperationType.ADD, "endBound" : BoundingType.UP_TO_SURFACE, "oppositeDirection" : true, "depth" : 25.4 * mm, "endBoundEntityFace" : qUnion([Q1]), "offsetDistance" : 25.4 * mm});
        }
        {
            var Q0;
            Q0=makeQuery(id+"F3.boolean.opBoolean","MERGE",FACE,{"derivedFrom":[makeQuery(id+"F1.opExtrude","CAP_FACE",FACE,{"disambiguationData":[OSD([sQuery(id+"F0.wireOp",EDGE,"E0"),sQuery(id+"F0.wireOp",EDGE,"E1"),sQuery(id+"F0.wireOp",EDGE,"E2"),sQuery(id+"F0.wireOp",EDGE,"E3"),sQuery(id+"F0.wireOp",EDGE,"E4"),sQuery(id+"F0.wireOp",EDGE,"E5"),sQuery(id+"F0.wireOp",EDGE,"E6"),sQuery(id+"F0.wireOp",EDGE,"E7"),sQuery(id+"F0.wireOp",EDGE,"E8"),sQuery(id+"F0.wireOp",EDGE,"E9"),sQuery(id+"F0.wireOp",EDGE,"E10"),sQuery(id+"F0.wireOp",EDGE,"E11"),sQuery(id+"F0.wireOp",EDGE,"E12"),sQuery(id+"F0.wireOp",EDGE,"E13"),sQuery(id+"F0.wireOp",EDGE,"E14"),sQuery(id+"F0.wireOp",EDGE,"E15"),sQuery(id+"F0.wireOp",EDGE,"E16"),sQuery(id+"F0.wireOp",EDGE,"E17")])],"isStart":false}),makeQuery(id+"F3.opExtrude","CAP_FACE",FACE,{"disambiguationData":[OSD([sQuery(id+"F2.wireOp",EDGE,"E18"),sQuery(id+"F2.wireOp",EDGE,"E19.0")])],"isStart":true})]});
            var sketch = newSketch(context, id + "F4", { "sketchPlane" : qUnion([Q0])});
            skFitSpline(sketch, "E20", {"points": [v(14.71, 11.5) * mm, v(13.85, 11.6) * mm, v(13, 11.6) * mm, v(12.21, 10.94) * mm, v(13.36, 9.74) * mm, v(14.36, 9.04) * mm, v(15.26, 8.98) * mm, v(15.46, 9.87) * mm, v(14.87, 10.8) * mm, v(14.71, 11.5) * mm]});
            skSolve(sketch);
        }
        {
            var Q0;
            Q0 = qSketchRegion(id + "F4", true);
            extrude(context, id + "F5", {"entities" : qUnion([Q0]), "operationType" : NewBodyOperationType.REMOVE, "oppositeDirection" : true, "depth" : 25.4 * mm, "offsetDistance" : 25.4 * mm});
        }
    });
